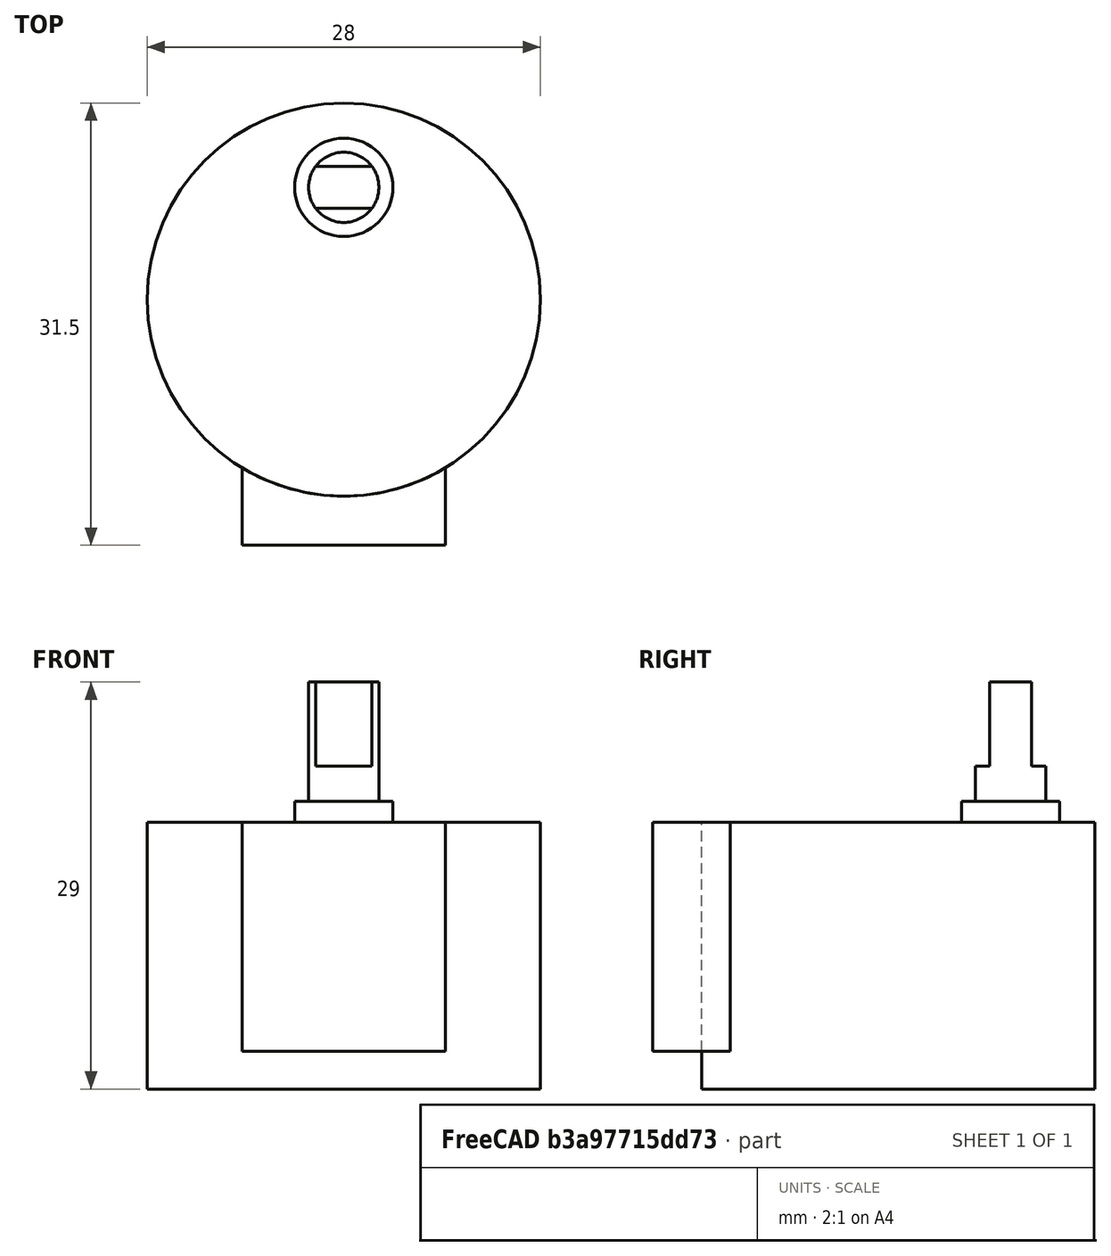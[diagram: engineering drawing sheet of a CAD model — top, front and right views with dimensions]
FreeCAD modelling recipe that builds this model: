
FCSTD DOCUMENT  (FreeCAD 0.16R6712 (Git))
Label: 28BYJ-48
License: All rights reserved
LicenseURL: http://en.wikipedia.org/wiki/All_rights_reserved
objects: Part::Cylinder×4, Part::Box×3, Part::Cut×3, Part::Part2DObjectPython×3, Part::RuledSurface×1, Part::Fuse×1, Part::MultiCommon×1
note: 16 computed .brp shape members not serialized (recipe doc carries the construction recipe); baked Part::Feature solids carry a one-line shape summary decoded from their .brp

FEATURE [Part::Cylinder] Cylinder
  Angle = 360
  Height = 19
  Radius = 14
FEATURE [Part::Box] Box  label="Cube"
  Height = 16.3
  Length = 17.5
  Placement = pos=(0,-7.25,2.7) rot=(0,0,1;0rad)
  Width = 14.5
FEATURE [Part::Cylinder] Cylinder001
  Angle = 360
  Height = 19
  Radius = 14
FEATURE [Part::Cut] Cut
  Base = -> Box
  Placement = pos=(0,0,0) rot=(0,0,-1;1.5708rad)
  Tool = -> Cylinder001
FEATURE [Part::Cylinder] Cylinder002
  Angle = 360
  Height = 8.5
  Placement = pos=(0,0,20.5) rot=(0,0,1;0rad)
  Radius = 2.5
FEATURE [Part::Box] Box001  label="Cube001"
  Height = 4
  Length = 5
  Placement = pos=(-2.5,-2.5,19) rot=(0,0,1;0rad)
  Width = 5
FEATURE [Part::Box] Box002  label="Cube002"
  Height = 6
  Length = 5
  Placement = pos=(-2.5,-1.5,23) rot=(0,0,1;0rad)
  Width = 3
FEATURE [Part::Cylinder] Cylinder003
  Angle = 360
  Height = 1.5
  Placement = pos=(0,8,19) rot=(0,0,1;0rad)
  Radius = 3.5
FEATURE [Part::Part2DObjectPython] Arc  # Draft 2D object (typed FeaturePython)
  FirstAngle = 90
  LastAngle = 270
  MakeFace = true
  Placement = pos=(-17.5,0,19) rot=(0,0,1;0rad)
  Radius = 3.5
FEATURE [Part::Part2DObjectPython] Arc001  # Draft 2D object (typed FeaturePython)
  FirstAngle = 165.52
  LastAngle = 194.48
  MakeFace = true
  Placement = pos=(0,0,19) rot=(0,0,1;0rad)
  Radius = 14
FEATURE [Part::RuledSurface] Ruled_Surface
  Curve1 = -> Arc [Edge1]
  Curve2 = -> Arc001 [Edge1]
  Orientation = 0
FEATURE [Part::Part2DObjectPython] Circle  # Draft 2D object (typed FeaturePython)
  FirstAngle = 0
  LastAngle = 0
  MakeFace = true
  Placement = pos=(-17.5,0,19) rot=(0,0,1;0rad)
  Radius = 2.1
FEATURE [Part::Cut] Cut001
  Base = -> Ruled_Surface
  Placement = pos=(0,0,0) rot=(0,0,1;3.14159rad)
  Tool = -> Circle
FEATURE [Part::Cut] Cut002
  Base = -> Ruled_Surface
  Tool = -> Circle
FEATURE [Part::Fuse] Fusion
  Base = -> Box001
  Tool = -> Box002
FEATURE [Part::MultiCommon] Common
  Placement = pos=(0,8,0) rot=(0,0,1;0rad)
  Shapes = -> [Cylinder002,Fusion]
